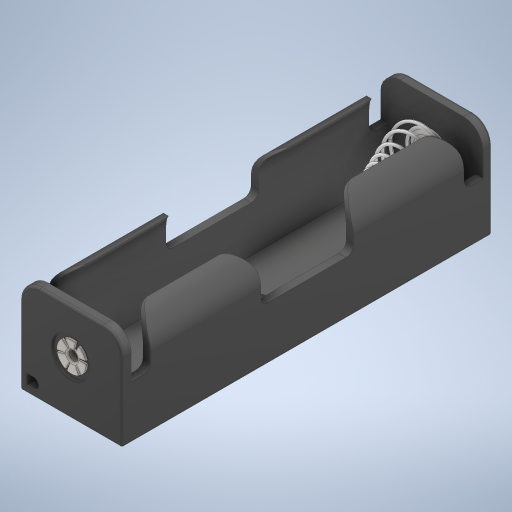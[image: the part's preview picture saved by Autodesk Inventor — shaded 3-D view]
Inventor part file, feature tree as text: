
AUTODESK INVENTOR PART (.ipt)
format: ipt  version: 2023 (Build 270158000, 158)  size: 1,575,424 bytes
history: imported  units: in
note: dims shown in document units (in); Inventor stores cm internally (conversion verified against a paired STEP export)
features: imported_body x1
ambient origin geometry x8: Origin, YZ Plane, XZ Plane, XY Plane, X Axis, Y Axis, Z Axis, Center Point
bodies: Solid1 (imported_parasolid), Solid2 (imported_parasolid), Solid3 (imported_parasolid), Solid4 (imported_parasolid), Solid5 (imported_parasolid), Solid6 (imported_parasolid), Solid7 (imported_parasolid), Solid8 (imported_parasolid), Body1 (imported_parasolid), Body2 (imported_parasolid), Body3 (imported_parasolid), Body4 (imported_parasolid), Body5 (imported_parasolid), Body6 (imported_parasolid), Body7 (imported_parasolid), Body8 (imported_parasolid)
feature tree (1):
  imported_body  NMx_Import_Brep_tag  [imported B-rep: ~14 faces, bbox_mm=None]
